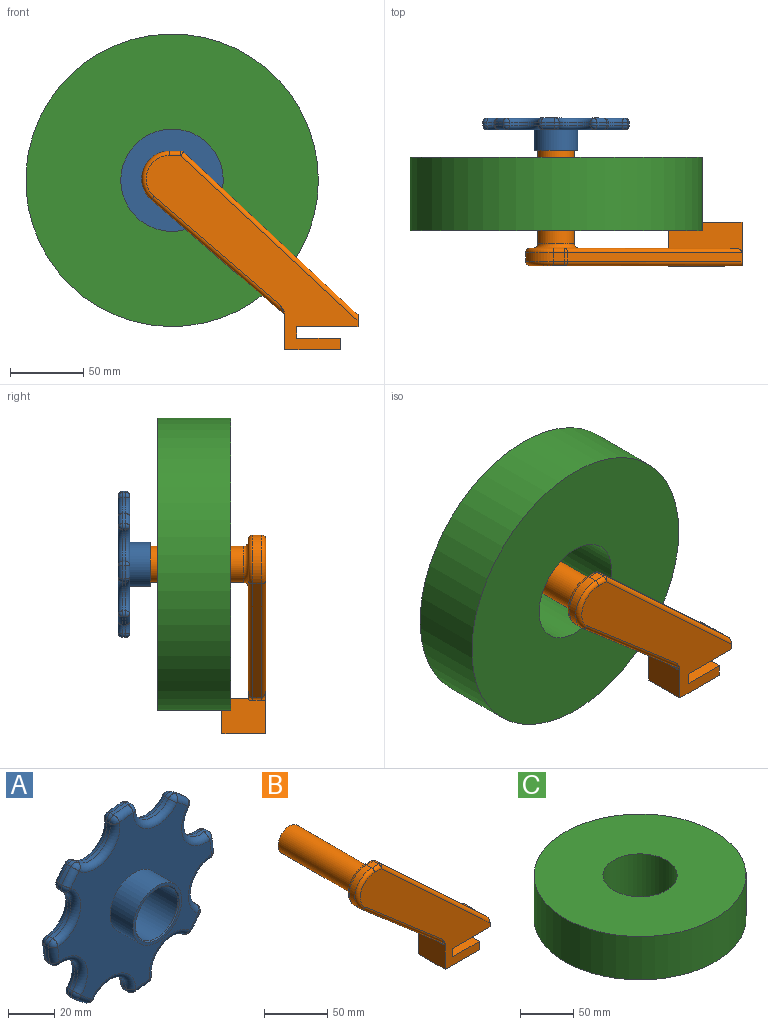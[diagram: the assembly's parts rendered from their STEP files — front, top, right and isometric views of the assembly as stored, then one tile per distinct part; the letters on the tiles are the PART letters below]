
ASSEMBLY  parts=3 mates=2
PART A: 105 faces, bbox 100.4x22x100.4 mm
  f0: cylinder r=50mm len=6.87mm, axis (0,1,0), area 17.7mm2, adj f48,f54,f64,f67
  f1: cylinder r=50mm len=8.77mm, axis (0,1,0), area 17.7mm2, adj f43,f49,f70,f73
  f2: cylinder r=50mm len=6.87mm, axis (0,1,0), area 17.7mm2, adj f38,f44,f76,f79
  f3: cylinder r=50mm len=8.77mm, axis (0,1,0), area 17.7mm2, adj f33,f39,f82,f85
  f4: cylinder r=50mm len=6.87mm, axis (0,1,0), area 17.7mm2, adj f28,f34,f88,f91
  f5: cylinder r=50mm len=8.77mm, axis (0,1,0), area 17.7mm2, adj f23,f29,f94,f97
  f6: cylinder r=50mm len=6.87mm, axis (0,1,0), area 17.7mm2, adj f18,f24,f100,f103
  f7: cylinder r=50mm len=8.77mm, axis (0,1,0), area 17.7mm2, adj f19,f53,f58,f61
  f8: cylinder r=12.95mm len=25.9mm, axis (0,1,0), area 1586.7mm2, adj f12,f56
  f9: cylinder r=14.95mm len=29.9mm, axis (0,1,0), area 1878.7mm2, adj f10,f11
  f10: plane 29.9x29.9mm, normal (0,-1,0), area 133.8mm2, adj f9,f56
  f11: plane 30x30mm, normal (0,-1,0), area 4.7mm2, adj f9,f13
  f12: plane 25.9x25.9mm, normal (0,-1,0), area 526.9mm2, adj f8
  f13: cylinder r=15mm len=30mm, axis (0,1,0), area 565.5mm2, adj f11,f14
  f14: plane 93.98x93.98mm, normal (0,-1,0), area 4293mm2, adj f13,f20,f25,f30,f35,f40,f45,f50
  f15: plane 93.98x93.98mm, normal (0,1,0), area 4999.8mm2, adj f17,f22,f27,f32,f37,f42,f47,f52
  f16: cylinder r=12mm len=21.62mm, axis (0,1,0), area 58.5mm2, adj f17,f18,f19,f20
  f17: torus R=15mm, axis (0,1,0), area 150.5mm2, adj f15,f16,f57,f101
  f18: cylinder r=3mm len=4.08mm, axis (0,-1,0), area 9.1mm2, adj f6,f16,f101,f104
  f19: cylinder r=3mm len=3.05mm, axis (0,-1,0), area 9.1mm2, adj f7,f16,f57,f60
  f20: torus R=15mm, axis (0,1,0), area 150.5mm2, adj f14,f16,f60,f104
  f21: cylinder r=12mm len=19.91mm, axis (0,1,0), area 58.5mm2, adj f22,f23,f24,f25
  f22: torus R=15mm, axis (0,1,0), area 150.5mm2, adj f15,f21,f95,f99
  f23: cylinder r=3mm len=3.39mm, axis (0,-1,0), area 9.1mm2, adj f5,f21,f95,f98
  f24: cylinder r=3mm len=4.14mm, axis (0,-1,0), area 9.1mm2, adj f6,f21,f99,f102
  f25: torus R=15mm, axis (0,1,0), area 150.5mm2, adj f14,f21,f98,f102
  f26: cylinder r=12mm len=21.62mm, axis (0,1,0), area 58.5mm2, adj f27,f28,f29,f30
  f27: torus R=15mm, axis (0,1,0), area 150.5mm2, adj f15,f26,f89,f93
  f28: cylinder r=3mm len=4.08mm, axis (0,-1,0), area 9.1mm2, adj f4,f26,f89,f92
  f29: cylinder r=3mm len=3.05mm, axis (0,-1,0), area 9.1mm2, adj f5,f26,f93,f96
  f30: torus R=15mm, axis (0,1,0), area 150.5mm2, adj f14,f26,f92,f96
  f31: cylinder r=12mm len=19.91mm, axis (0,1,0), area 58.5mm2, adj f32,f33,f34,f35
  f32: torus R=15mm, axis (0,1,0), area 150.5mm2, adj f15,f31,f83,f87
  f33: cylinder r=3mm len=3.39mm, axis (0,-1,0), area 9.1mm2, adj f3,f31,f83,f86
  f34: cylinder r=3mm len=4.14mm, axis (0,-1,0), area 9.1mm2, adj f4,f31,f87,f90
  f35: torus R=15mm, axis (0,1,0), area 150.5mm2, adj f14,f31,f86,f90
  f36: cylinder r=12mm len=21.62mm, axis (0,1,0), area 58.5mm2, adj f37,f38,f39,f40
  f37: torus R=15mm, axis (0,1,0), area 150.5mm2, adj f15,f36,f77,f81
  f38: cylinder r=3mm len=4.08mm, axis (0,-1,0), area 9.1mm2, adj f2,f36,f77,f80
  f39: cylinder r=3mm len=3.05mm, axis (0,-1,0), area 9.1mm2, adj f3,f36,f81,f84
  f40: torus R=15mm, axis (0,1,0), area 150.5mm2, adj f14,f36,f80,f84
  f41: cylinder r=12mm len=19.91mm, axis (0,1,0), area 58.5mm2, adj f42,f43,f44,f45
  f42: torus R=15mm, axis (0,1,0), area 150.5mm2, adj f15,f41,f71,f75
  f43: cylinder r=3mm len=3.39mm, axis (0,-1,0), area 9.1mm2, adj f1,f41,f71,f74
  f44: cylinder r=3mm len=4.14mm, axis (0,-1,0), area 9.1mm2, adj f2,f41,f75,f78
  f45: torus R=15mm, axis (0,1,0), area 150.5mm2, adj f14,f41,f74,f78
  f46: cylinder r=12mm len=21.62mm, axis (0,1,0), area 58.5mm2, adj f47,f48,f49,f50
  f47: torus R=15mm, axis (0,1,0), area 150.5mm2, adj f15,f46,f65,f69
  f48: cylinder r=3mm len=4.08mm, axis (0,-1,0), area 9.1mm2, adj f0,f46,f65,f68
  f49: cylinder r=3mm len=3.05mm, axis (0,-1,0), area 9.1mm2, adj f1,f46,f69,f72
  f50: torus R=15mm, axis (0,1,0), area 150.5mm2, adj f14,f46,f68,f72
  f51: cylinder r=12mm len=19.91mm, axis (0,1,0), area 58.5mm2, adj f52,f53,f54,f55
  f52: torus R=15mm, axis (0,1,0), area 150.5mm2, adj f15,f51,f59,f63
  f53: cylinder r=3mm len=3.39mm, axis (0,-1,0), area 9.1mm2, adj f7,f51,f59,f62
  f54: cylinder r=3mm len=4.14mm, axis (0,-1,0), area 9.1mm2, adj f0,f51,f63,f66
  f55: torus R=15mm, axis (0,1,0), area 150.5mm2, adj f14,f51,f62,f66
  f56: cone r=13.45mm half-angle=45deg, axis (0,-1,0), area 58.6mm2, adj f8,f10
  f57: sphere r=3mm, area 13.7mm2, adj f17,f19,f58
  f58: torus R=47mm, axis (0,1,0), area 40.7mm2, adj f7,f15,f57,f59
  f59: sphere r=3mm, area 13.7mm2, adj f52,f53,f58
  f60: sphere r=3mm, area 13.7mm2, adj f19,f20,f61
  f61: torus R=47mm, axis (0,1,0), area 40.7mm2, adj f7,f14,f60,f62
  f62: sphere r=3mm, area 13.7mm2, adj f53,f55,f61
  f63: sphere r=3mm, area 13.7mm2, adj f52,f54,f64
  f64: torus R=47mm, axis (0,1,0), area 40.7mm2, adj f0,f15,f63,f65
  f65: sphere r=3mm, area 13.7mm2, adj f47,f48,f64
  f66: sphere r=3mm, area 13.7mm2, adj f54,f55,f67
  f67: torus R=47mm, axis (0,1,0), area 40.7mm2, adj f0,f14,f66,f68
  f68: sphere r=3mm, area 13.7mm2, adj f48,f50,f67
  f69: sphere r=3mm, area 13.7mm2, adj f47,f49,f70
  f70: torus R=47mm, axis (0,1,0), area 40.7mm2, adj f1,f15,f69,f71
  f71: sphere r=3mm, area 13.7mm2, adj f42,f43,f70
  f72: sphere r=3mm, area 13.7mm2, adj f49,f50,f73
  f73: torus R=47mm, axis (0,1,0), area 40.7mm2, adj f1,f14,f72,f74
  f74: sphere r=3mm, area 13.7mm2, adj f43,f45,f73
  f75: sphere r=3mm, area 13.7mm2, adj f42,f44,f76
  f76: torus R=47mm, axis (0,1,0), area 40.7mm2, adj f2,f15,f75,f77
  f77: sphere r=3mm, area 13.7mm2, adj f37,f38,f76
  f78: sphere r=3mm, area 13.7mm2, adj f44,f45,f79
  f79: torus R=47mm, axis (0,1,0), area 40.7mm2, adj f2,f14,f78,f80
  f80: sphere r=3mm, area 13.7mm2, adj f38,f40,f79
  f81: sphere r=3mm, area 13.7mm2, adj f37,f39,f82
  f82: torus R=47mm, axis (0,1,0), area 40.7mm2, adj f3,f15,f81,f83
  f83: sphere r=3mm, area 13.7mm2, adj f32,f33,f82
  f84: sphere r=3mm, area 13.7mm2, adj f39,f40,f85
  f85: torus R=47mm, axis (0,1,0), area 40.7mm2, adj f3,f14,f84,f86
  f86: sphere r=3mm, area 13.7mm2, adj f33,f35,f85
  f87: sphere r=3mm, area 13.7mm2, adj f32,f34,f88
  f88: torus R=47mm, axis (0,1,0), area 40.7mm2, adj f4,f15,f87,f89
  f89: sphere r=3mm, area 13.7mm2, adj f27,f28,f88
  f90: sphere r=3mm, area 13.7mm2, adj f34,f35,f91
  f91: torus R=47mm, axis (0,1,0), area 40.7mm2, adj f4,f14,f90,f92
  f92: sphere r=3mm, area 13.7mm2, adj f28,f30,f91
  f93: sphere r=3mm, area 13.7mm2, adj f27,f29,f94
  f94: torus R=47mm, axis (0,1,0), area 40.7mm2, adj f5,f15,f93,f95
  f95: sphere r=3mm, area 13.7mm2, adj f22,f23,f94
  f96: sphere r=3mm, area 13.7mm2, adj f29,f30,f97
  f97: torus R=47mm, axis (0,1,0), area 40.7mm2, adj f5,f14,f96,f98
  f98: sphere r=3mm, area 13.7mm2, adj f23,f25,f97
  f99: sphere r=3mm, area 13.7mm2, adj f22,f24,f100
  f100: torus R=47mm, axis (0,1,0), area 40.7mm2, adj f6,f15,f99,f101
  f101: sphere r=3mm, area 13.7mm2, adj f17,f18,f100
  f102: sphere r=3mm, area 13.7mm2, adj f24,f25,f103
  f103: torus R=47mm, axis (0,1,0), area 40.7mm2, adj f6,f14,f102,f104
  f104: sphere r=3mm, area 13.7mm2, adj f18,f20,f103
PART B: 32 faces, bbox 153x101.6x139.2 mm
  f0: plane 42x30mm, normal (0,0,-1), area 1260mm2, adj f1,f4,f5,f25
  f1: plane 146.43x134.6mm, normal (0,-1,0), area 5394mm2, adj f0,f4,f6,f10,f11,f12,f21,f22
  f2: plane 140.44x109mm, normal (0,1,0), area 3880.2mm2, adj f3,f14,f16,f18,f19,f24,f31
  f3: plane 51.36x22.35mm, normal (0,0,1), area 902.8mm2, adj f2,f4,f5,f6,f18,f19
  f4: plane 31.18x9.18mm, normal (1,0,0), area 237.4mm2, adj f0,f1,f3,f5,f9,f11
  f5: plane 50x24mm, normal (0,1,0), area 768mm2, adj f0,f3,f4,f6,f25,f26,f27,f28
  f6: plane 30x24mm, normal (-1,0,0), area 705.5mm2, adj f1,f3,f5,f19,f20,f21,f26
  f7: plane 7.65x6mm, normal (0,0,1), area 45.9mm2, adj f12,f15,f16,f23
  f8: plane 90.2x77.71mm, normal (-0.65,0,-0.76), area 714.3mm2, adj f10,f14,f20,f23
  f9: plane 119.14x111.19mm, normal (0.68,0,0.73), area 977.8mm2, adj f4,f11,f15,f18
  f10: cylinder r=3mm len=92.15mm, axis (0.76,0,-0.65), area 548.9mm2, adj f1,f8,f21,f22
  f11: cylinder r=3mm len=123.23mm, axis (-0.73,0,0.68), area 774.5mm2, adj f1,f4,f9,f13
  f12: cylinder r=3mm len=7.65mm, axis (-1,0,0), area 36.1mm2, adj f1,f7,f13,f22
  f13: sphere r=3mm, area 8.7mm2, adj f11,f12,f15
  f14: cylinder r=3mm len=92.15mm, axis (-0.76,0,0.65), area 548.9mm2, adj f2,f8,f19,f24
  f15: cylinder r=3mm len=6mm, axis (0,1,0), area 13.5mm2, adj f7,f9,f13,f17
  f16: cylinder r=3mm len=7.65mm, axis (-1,0,0), area 36.1mm2, adj f2,f7,f17,f24
  f17: sphere r=3mm, area 8.7mm2, adj f15,f16,f18
  f18: cylinder r=3mm len=121.18mm, axis (0.73,0,-0.68), area 760.4mm2, adj f2,f3,f9,f17
  f19: bspline ~7.92x6mm, area 12.4mm2, adj f2,f3,f6,f14,f20
  f20: cylinder r=3mm len=6mm, axis (0,-1,0), area 15.5mm2, adj f6,f8,f19,f21
  f21: bspline ~7.92x6mm, area 16.1mm2, adj f1,f6,f10,f20
  f22: torus R=16mm, axis (0,-1,0), area 205.1mm2, adj f1,f10,f12,f23
  f23: cylinder r=19mm len=33.39mm, axis (0,1,0), area 277.1mm2, adj f7,f8,f22,f24
  f24: torus R=16mm, axis (0,-1,0), area 205.1mm2, adj f2,f14,f16,f23
  f25: plane 30x8mm, normal (1,0,0), area 240mm2, adj f0,f1,f5,f28
  f26: plane 38x30mm, normal (0,0,-1), area 1140mm2, adj f1,f5,f6,f27
  f27: plane 30x8mm, normal (1,0,0), area 240mm2, adj f1,f5,f26,f28
  f28: plane 30x30mm, normal (0,0,1), area 900mm2, adj f1,f5,f25,f27
  f29: cylinder r=12.5mm len=82mm, axis (0,-1,0), area 6440.3mm2, adj f30,f31
  f30: plane 25x25mm, normal (0,1,0), area 490.9mm2, adj f29
  f31: torus R=15.5mm, axis (0,-1,0), area 402.4mm2, adj f2,f29
PART C: 4 faces, bbox 200x200x50 mm
  f0: cylinder r=35mm len=70mm, axis (0,0,-1), area 10995.6mm2, adj f2,f3
  f1: cylinder r=100mm len=200mm, axis (0,0,-1), area 31415.9mm2, adj f2,f3
  f2: plane 200x200mm, normal (0,0,1), area 27567.5mm2, adj f0,f1
  f3: plane 200x200mm, normal (0,0,-1), area 27567.5mm2, adj f0,f1
PLACE A t=(-1.1,-36.5,28.11)mm
PLACE B t=(-1.1,-38.41,28.11)mm fixed
PLACE C rot(axis=(1,0,0),90deg) t=(-128.22,35.62,128.11)mm
MATE slider B.f31 <-> C.f0  axis (0,-1,0) through (-128.22,17.59,128.11)mm
MATE slider B.f31 <-> A.f8  axis (0,-1,0) through (-128.22,17.59,128.11)mm
